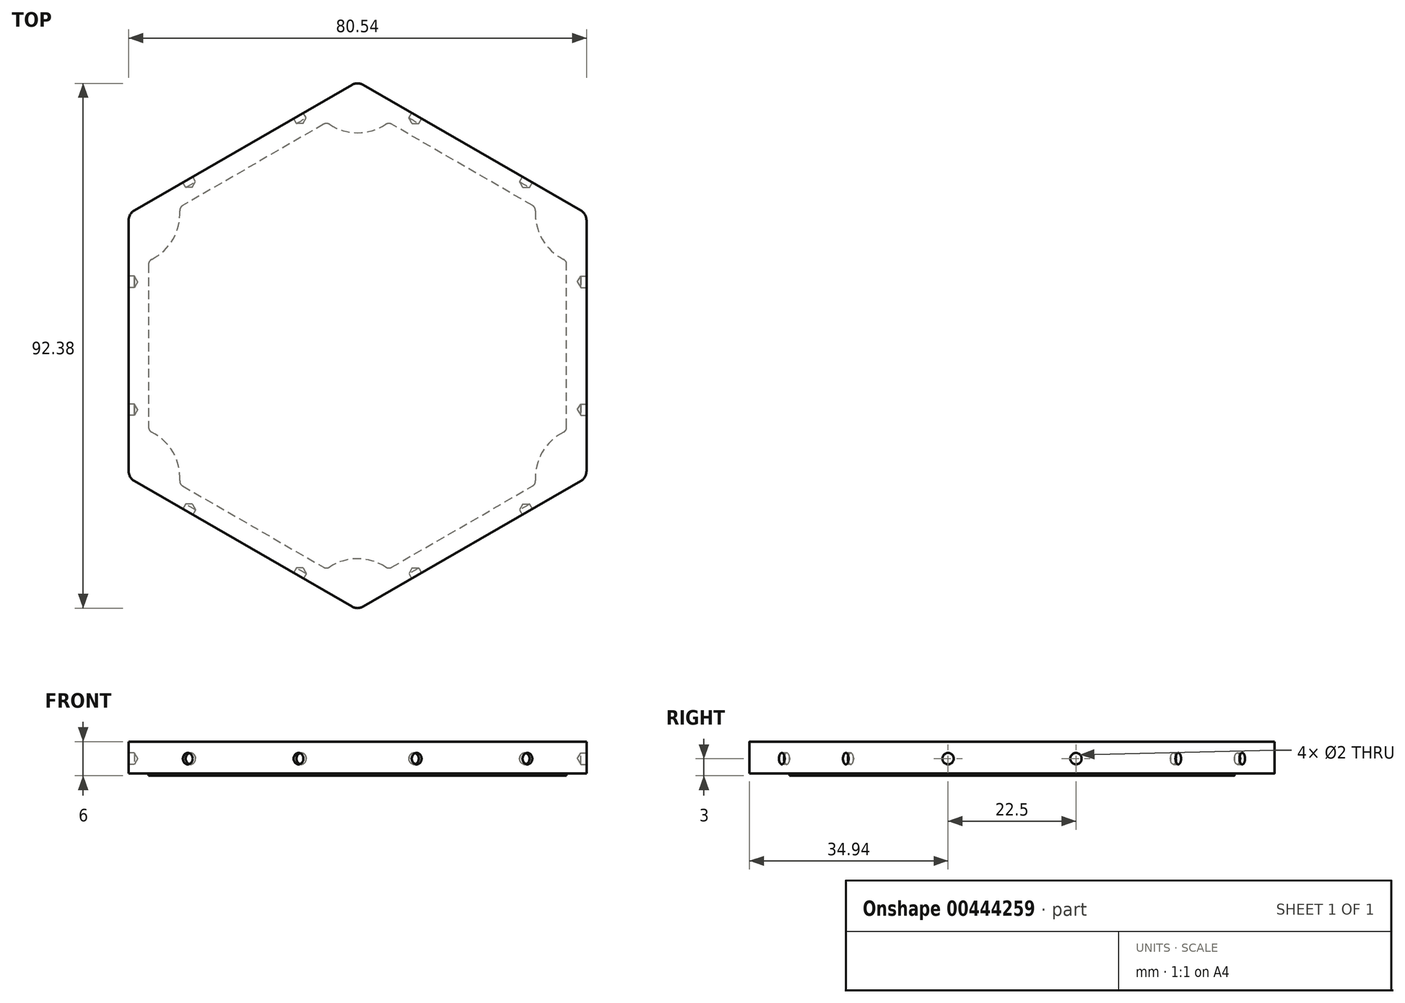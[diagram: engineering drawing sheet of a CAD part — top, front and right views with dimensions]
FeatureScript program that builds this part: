
annotation { "Feature Type Name" : "Feature", "Feature Type Description" : "" }
export const myFeature = defineFeature(function(context is Context, id is Id, definition is map)
    precondition{}
    {
        {
            var Q0;
            Q0=qCreatedBy(makeId("Top.planeOp"),FACE);
            var sketch = newSketch(context, id + "F0", { "sketchPlane" : qUnion([Q0])});
            skCircle(sketch, "E0.cCircle", {"center": v(0, 0) * mm, "radius": 46.5 * mm, "construction": true});
            skLineSegment(sketch, "E0.0", {"start": v(0, 46.5) * mm, "end": v(40.27, 23.25) * mm});
            skLineSegment(sketch, "E0.1", {"start": v(40.27, 23.25) * mm, "end": v(40.27, -23.25) * mm});
            skLineSegment(sketch, "E0.2", {"start": v(40.27, -23.25) * mm, "end": v(0, -46.5) * mm});
            skLineSegment(sketch, "E0.3", {"start": v(0, -46.5) * mm, "end": v(-40.27, -23.25) * mm});
            skLineSegment(sketch, "E0.4", {"start": v(-40.27, -23.25) * mm, "end": v(-40.27, 23.25) * mm});
            skLineSegment(sketch, "E0.5", {"start": v(-40.27, 23.25) * mm, "end": v(0, 46.5) * mm});
            skSolve(sketch);
        }
        {
            var Q0;
            Q0=makeQuery(id+"F0.imprint","IMPRINT",FACE,{"disambiguationData":[TD([[makeQuery(id+"F0.imprint","IMPRINT",EDGE,{"derivedFrom":sQuery(id+"F0.wireOp",EDGE,"E0.0")}),-1.0]])]});
            extrude(context, id + "F1", {"entities" : qUnion([Q0]), "depth" : 6 * mm});
        }
        {
            var Q0;
            Q0=makeQuery(id+"F1.opExtrude","SWEPT_FACE",FACE,{"disambiguationData":[OSD([sQuery(id+"F0.wireOp",EDGE,"E0.4")])]});
            var sketch = newSketch(context, id + "F2", { "sketchPlane" : qUnion([Q0])});
            skPoint(sketch, "E1", {"position": v(-11.25, 3) * mm});
            skPoint(sketch, "E2.MirrorP", {"position": v(11.25, 3) * mm});
            skSolve(sketch);
        }
        {
            var Q0;
            Q0=sQuery(id+"F2.wireOp",VERTEX,"E1");
            var Q1;
            Q1=sQuery(id+"F2.wireOp",VERTEX,"E2.MirrorP");
            var Q2;
            Q2=makeQuery(id+"F1.opExtrude","SWEPT_BODY",BODY,{"disambiguationData":[OSD([sQuery(id+"F0.wireOp",EDGE,"E0.0"),sQuery(id+"F0.wireOp",EDGE,"E0.1"),sQuery(id+"F0.wireOp",EDGE,"E0.2"),sQuery(id+"F0.wireOp",EDGE,"E0.3"),sQuery(id+"F0.wireOp",EDGE,"E0.4"),sQuery(id+"F0.wireOp",EDGE,"E0.5")])]});
            hole(context, id + "F3", {"style" : HoleStyle.SIMPLE, "endStyle" : HoleEndStyle.BLIND, "holeDiameter" : 2 * mm, "holeDepth" : 1 * mm, "isTappedThrough" : true, "tappedDepth" : 12 * mm, "tapClearance" : 3, "startFromSketch" : true, "locations" : qUnion([Q0, Q1]), "scope" : qUnion([Q2])});
        }
        {
            var Q0;
            Q0=makeQuery(id+"F1.opExtrude","SWEPT_FACE",FACE,{"disambiguationData":[OSD([sQuery(id+"F0.wireOp",EDGE,"E0.0")])]});
            var sketch = newSketch(context, id + "F4", { "sketchPlane" : qUnion([Q0])});
            skPoint(sketch, "E3", {"position": v(-11.25, 3) * mm});
            skPoint(sketch, "E4.MirrorP", {"position": v(11.25, 3) * mm});
            skSolve(sketch);
        }
        {
            var Q0;
            Q0=makeQuery(id+"F1.opExtrude","SWEPT_FACE",FACE,{"disambiguationData":[OSD([sQuery(id+"F0.wireOp",EDGE,"E0.1")])]});
            var sketch = newSketch(context, id + "F5", { "sketchPlane" : qUnion([Q0])});
            skPoint(sketch, "E5", {"position": v(-11.25, 3) * mm});
            skPoint(sketch, "E6.MirrorP", {"position": v(11.25, 3) * mm});
            skSolve(sketch);
        }
        {
            var Q0;
            Q0=makeQuery(id+"F1.opExtrude","SWEPT_FACE",FACE,{"disambiguationData":[OSD([sQuery(id+"F0.wireOp",EDGE,"E0.2")])]});
            var sketch = newSketch(context, id + "F6", { "sketchPlane" : qUnion([Q0])});
            skPoint(sketch, "E7", {"position": v(-11.25, 3) * mm});
            skPoint(sketch, "E8.MirrorP", {"position": v(11.25, 3) * mm});
            skSolve(sketch);
        }
        {
            var Q0;
            Q0=makeQuery(id+"F1.opExtrude","SWEPT_FACE",FACE,{"disambiguationData":[OSD([sQuery(id+"F0.wireOp",EDGE,"E0.3")])]});
            var sketch = newSketch(context, id + "F7", { "sketchPlane" : qUnion([Q0])});
            skPoint(sketch, "E9", {"position": v(-11.25, 3) * mm});
            skPoint(sketch, "E10.MirrorP", {"position": v(11.25, 3) * mm});
            skSolve(sketch);
        }
        {
            var Q0;
            Q0=makeQuery(id+"F1.opExtrude","SWEPT_FACE",FACE,{"disambiguationData":[OSD([sQuery(id+"F0.wireOp",EDGE,"E0.5")])]});
            var sketch = newSketch(context, id + "F8", { "sketchPlane" : qUnion([Q0])});
            skPoint(sketch, "E11", {"position": v(-11.25, 3) * mm});
            skPoint(sketch, "E12.MirrorP", {"position": v(11.25, 3) * mm});
            skSolve(sketch);
        }
        {
            var Q0;
            Q0=sQuery(id+"F8.wireOp",VERTEX,"E11");
            var Q1;
            Q1=sQuery(id+"F8.wireOp",VERTEX,"E12.MirrorP");
            var Q2;
            Q2=sQuery(id+"F4.wireOp",VERTEX,"E4.MirrorP");
            var Q3;
            Q3=sQuery(id+"F4.wireOp",VERTEX,"E3");
            var Q4;
            Q4=sQuery(id+"F5.wireOp",VERTEX,"E6.MirrorP");
            var Q5;
            Q5=sQuery(id+"F5.wireOp",VERTEX,"E5");
            var Q6;
            Q6=sQuery(id+"F6.wireOp",VERTEX,"E8.MirrorP");
            var Q7;
            Q7=sQuery(id+"F6.wireOp",VERTEX,"E7");
            var Q8;
            Q8=sQuery(id+"F7.wireOp",VERTEX,"E9");
            var Q9;
            Q9=sQuery(id+"F7.wireOp",VERTEX,"E10.MirrorP");
            var Q10;
            Q10=makeQuery(id+"F1.opExtrude","SWEPT_BODY",BODY,{"disambiguationData":[OSD([sQuery(id+"F0.wireOp",EDGE,"E0.0"),sQuery(id+"F0.wireOp",EDGE,"E0.1"),sQuery(id+"F0.wireOp",EDGE,"E0.2"),sQuery(id+"F0.wireOp",EDGE,"E0.3"),sQuery(id+"F0.wireOp",EDGE,"E0.4"),sQuery(id+"F0.wireOp",EDGE,"E0.5")])]});
            hole(context, id + "F9", {"style" : HoleStyle.SIMPLE, "endStyle" : HoleEndStyle.BLIND, "holeDiameter" : 2 * mm, "holeDepth" : 1 * mm, "isTappedThrough" : true, "tappedDepth" : 12 * mm, "tapClearance" : 3, "startFromSketch" : true, "locations" : qUnion([Q0, Q1, Q2, Q3, Q4, Q5, Q6, Q7, Q8, Q9]), "scope" : qUnion([Q10])});
        }
        {
            var Q0;
            Q0=makeQuery(id+"F1.opExtrude","SWEPT_EDGE",EDGE,{"disambiguationData":[OSD([sQuery(id+"F0.wireOp",EDGE,"E0.4"),sQuery(id+"F0.wireOp",EDGE,"E0.5")])]});
            var Q1;
            Q1=makeQuery(id+"F1.opExtrude","SWEPT_EDGE",EDGE,{"disambiguationData":[OSD([sQuery(id+"F0.wireOp",EDGE,"E0.0"),sQuery(id+"F0.wireOp",EDGE,"E0.5")])]});
            var Q2;
            Q2=makeQuery(id+"F1.opExtrude","SWEPT_EDGE",EDGE,{"disambiguationData":[OSD([sQuery(id+"F0.wireOp",EDGE,"E0.0"),sQuery(id+"F0.wireOp",EDGE,"E0.1")])]});
            var Q3;
            Q3=makeQuery(id+"F1.opExtrude","SWEPT_EDGE",EDGE,{"disambiguationData":[OSD([sQuery(id+"F0.wireOp",EDGE,"E0.1"),sQuery(id+"F0.wireOp",EDGE,"E0.2")])]});
            var Q4;
            Q4=makeQuery(id+"F1.opExtrude","SWEPT_EDGE",EDGE,{"disambiguationData":[OSD([sQuery(id+"F0.wireOp",EDGE,"E0.3"),sQuery(id+"F0.wireOp",EDGE,"E0.4")])]});
            var Q5;
            Q5=makeQuery(id+"F1.opExtrude","SWEPT_EDGE",EDGE,{"disambiguationData":[OSD([sQuery(id+"F0.wireOp",EDGE,"E0.2"),sQuery(id+"F0.wireOp",EDGE,"E0.3")])]});
            fillet(context, id + "F10", {"entities" : qUnion([Q0, Q1, Q2, Q3, Q4, Q5]), "radius" : 2 * mm, "tangentPropagation" : true, "allowEdgeOverflow" : false});
        }
        {
            var Q0;
            Q0=qCreatedBy(makeId("Top.planeOp"),FACE);
            var sketch = newSketch(context, id + "F11", { "sketchPlane" : qUnion([Q0])});
            skCircle(sketch, "E13", {"center": v(0, -46.5) * mm, "radius": 9 * mm});
            skCircle(sketch, "E14.1.0", {"center": v(40.27, -23.25) * mm, "radius": 9 * mm});
            skCircle(sketch, "E14.2.0", {"center": v(40.27, 23.25) * mm, "radius": 9 * mm});
            skCircle(sketch, "E14.3.0", {"center": v(0, 46.5) * mm, "radius": 9 * mm});
            skCircle(sketch, "E14.4.0", {"center": v(-40.27, 23.25) * mm, "radius": 9 * mm});
            skCircle(sketch, "E14.5.0", {"center": v(-40.27, -23.25) * mm, "radius": 9 * mm});
            skPoint(sketch, "E14.center", {"position": v(0, 0) * mm});
            skLineSegment(sketch, "E15.bottom", {"start": v(36.77, -20) * mm, "end": v(40.27, -20) * mm});
            skLineSegment(sketch, "E15.top", {"start": v(36.77, 20) * mm, "end": v(40.27, 20) * mm});
            skLineSegment(sketch, "E15.left", {"start": v(36.77, -20) * mm, "end": v(36.77, 20) * mm});
            skLineSegment(sketch, "E15.right", {"start": v(40.27, -20) * mm, "end": v(40.27, 20) * mm});
            skLineSegment(sketch, "E16.1.0", {"start": v(35.7, 21.84) * mm, "end": v(37.46, 24.88) * mm});
            skLineSegment(sketch, "E16.1.1", {"start": v(37.46, 24.87) * mm, "end": v(2.81, 44.88) * mm});
            skLineSegment(sketch, "E16.1.2", {"start": v(35.7, 21.84) * mm, "end": v(1.06, 41.84) * mm});
            skLineSegment(sketch, "E16.1.3", {"start": v(1.06, 41.84) * mm, "end": v(2.81, 44.88) * mm});
            skLineSegment(sketch, "E16.2.0", {"start": v(-1.06, 41.84) * mm, "end": v(-2.81, 44.88) * mm});
            skLineSegment(sketch, "E16.2.1", {"start": v(-2.81, 44.88) * mm, "end": v(-37.46, 24.88) * mm});
            skLineSegment(sketch, "E16.2.2", {"start": v(-1.06, 41.84) * mm, "end": v(-35.7, 21.84) * mm});
            skLineSegment(sketch, "E16.2.3", {"start": v(-35.7, 21.84) * mm, "end": v(-37.46, 24.88) * mm});
            skLineSegment(sketch, "E16.3.0", {"start": v(-36.77, 20) * mm, "end": v(-40.27, 20) * mm});
            skLineSegment(sketch, "E16.3.1", {"start": v(-40.27, 20) * mm, "end": v(-40.27, -20) * mm});
            skLineSegment(sketch, "E16.3.2", {"start": v(-36.77, 20) * mm, "end": v(-36.77, -20) * mm});
            skLineSegment(sketch, "E16.3.3", {"start": v(-36.77, -20) * mm, "end": v(-40.27, -20) * mm});
            skLineSegment(sketch, "E16.4.0", {"start": v(-35.7, -21.84) * mm, "end": v(-37.46, -24.88) * mm});
            skLineSegment(sketch, "E16.4.1", {"start": v(-37.46, -24.87) * mm, "end": v(-2.81, -44.88) * mm});
            skLineSegment(sketch, "E16.4.2", {"start": v(-35.7, -21.84) * mm, "end": v(-1.06, -41.84) * mm});
            skLineSegment(sketch, "E16.4.3", {"start": v(-1.06, -41.84) * mm, "end": v(-2.81, -44.88) * mm});
            skLineSegment(sketch, "E16.5.0", {"start": v(1.06, -41.84) * mm, "end": v(2.81, -44.88) * mm});
            skLineSegment(sketch, "E16.5.1", {"start": v(2.81, -44.88) * mm, "end": v(37.46, -24.88) * mm});
            skLineSegment(sketch, "E16.5.2", {"start": v(1.06, -41.84) * mm, "end": v(35.7, -21.84) * mm});
            skLineSegment(sketch, "E16.5.3", {"start": v(35.7, -21.84) * mm, "end": v(37.46, -24.88) * mm});
            skSolve(sketch);
        }
        {
            var Q0;
            Q0 = qSketchRegion(id + "F11", true);
            extrude(context, id + "F12", {"entities" : qUnion([Q0]), "operationType" : NewBodyOperationType.REMOVE, "depth" : 0.4 * mm});
        }
        {
            var Q0;
            Q0=makeQuery(id+"F12.boolean.opBoolean","COPY",EDGE,{"derivedFrom":makeQuery(id+"F12.opExtrude","SWEPT_EDGE",EDGE,{"disambiguationData":[OSD([sQuery(id+"F11.wireOp",EDGE,"E14.2.0"),sQuery(id+"F11.wireOp",EDGE,"E15.left")])]})});
            var Q1;
            Q1=makeQuery(id+"F12.boolean.opBoolean","COPY",EDGE,{"derivedFrom":makeQuery(id+"F12.opExtrude","SWEPT_EDGE",EDGE,{"disambiguationData":[OSD([sQuery(id+"F11.wireOp",EDGE,"E14.1.0"),sQuery(id+"F11.wireOp",EDGE,"E15.left")])]})});
            var Q2;
            Q2=makeQuery(id+"F12.boolean.opBoolean","COPY",EDGE,{"derivedFrom":makeQuery(id+"F12.opExtrude","SWEPT_EDGE",EDGE,{"disambiguationData":[OSD([sQuery(id+"F11.wireOp",EDGE,"E14.1.0"),sQuery(id+"F11.wireOp",EDGE,"E16.5.2")])]})});
            var Q3;
            Q3=makeQuery(id+"F12.boolean.opBoolean","COPY",EDGE,{"derivedFrom":makeQuery(id+"F12.opExtrude","SWEPT_EDGE",EDGE,{"disambiguationData":[OSD([sQuery(id+"F11.wireOp",EDGE,"E13"),sQuery(id+"F11.wireOp",EDGE,"E16.5.2")])]})});
            var Q4;
            Q4=makeQuery(id+"F12.boolean.opBoolean","COPY",EDGE,{"derivedFrom":makeQuery(id+"F12.opExtrude","SWEPT_EDGE",EDGE,{"disambiguationData":[OSD([sQuery(id+"F11.wireOp",EDGE,"E13"),sQuery(id+"F11.wireOp",EDGE,"E16.4.2")])]})});
            var Q5;
            Q5=makeQuery(id+"F12.boolean.opBoolean","COPY",EDGE,{"derivedFrom":makeQuery(id+"F12.opExtrude","SWEPT_EDGE",EDGE,{"disambiguationData":[OSD([sQuery(id+"F11.wireOp",EDGE,"E14.5.0"),sQuery(id+"F11.wireOp",EDGE,"E16.4.2")])]})});
            var Q6;
            Q6=makeQuery(id+"F12.boolean.opBoolean","COPY",EDGE,{"derivedFrom":makeQuery(id+"F12.opExtrude","SWEPT_EDGE",EDGE,{"disambiguationData":[OSD([sQuery(id+"F11.wireOp",EDGE,"E14.5.0"),sQuery(id+"F11.wireOp",EDGE,"E16.3.2")])]})});
            var Q7;
            Q7=makeQuery(id+"F12.boolean.opBoolean","COPY",EDGE,{"derivedFrom":makeQuery(id+"F12.opExtrude","SWEPT_EDGE",EDGE,{"disambiguationData":[OSD([sQuery(id+"F11.wireOp",EDGE,"E14.4.0"),sQuery(id+"F11.wireOp",EDGE,"E16.3.2")])]})});
            var Q8;
            Q8=makeQuery(id+"F12.boolean.opBoolean","COPY",EDGE,{"derivedFrom":makeQuery(id+"F12.opExtrude","SWEPT_EDGE",EDGE,{"disambiguationData":[OSD([sQuery(id+"F11.wireOp",EDGE,"E14.4.0"),sQuery(id+"F11.wireOp",EDGE,"E16.2.2")])]})});
            var Q9;
            Q9=makeQuery(id+"F12.boolean.opBoolean","COPY",EDGE,{"derivedFrom":makeQuery(id+"F12.opExtrude","SWEPT_EDGE",EDGE,{"disambiguationData":[OSD([sQuery(id+"F11.wireOp",EDGE,"E14.3.0"),sQuery(id+"F11.wireOp",EDGE,"E16.2.2")])]})});
            var Q10;
            Q10=makeQuery(id+"F12.boolean.opBoolean","COPY",EDGE,{"derivedFrom":makeQuery(id+"F12.opExtrude","SWEPT_EDGE",EDGE,{"disambiguationData":[OSD([sQuery(id+"F11.wireOp",EDGE,"E14.3.0"),sQuery(id+"F11.wireOp",EDGE,"E16.1.2")])]})});
            var Q11;
            Q11=makeQuery(id+"F12.boolean.opBoolean","COPY",EDGE,{"derivedFrom":makeQuery(id+"F12.opExtrude","SWEPT_EDGE",EDGE,{"disambiguationData":[OSD([sQuery(id+"F11.wireOp",EDGE,"E14.2.0"),sQuery(id+"F11.wireOp",EDGE,"E16.1.2")])]})});
            fillet(context, id + "F13", {"entities" : qUnion([Q0, Q1, Q2, Q3, Q4, Q5, Q6, Q7, Q8, Q9, Q10, Q11]), "radius" : 1 * mm, "tangentPropagation" : true, "allowEdgeOverflow" : false});
        }
    });
